# Revit family: Camera-Security-iPRO-2MP-Outdoor-PTZ-Network-Dome-AI-S65340-ZSeriesX
name_source: partatom
category: Security Devices
units: mm (PartAtom-declared; Revit-internal decimal feet)

## family parameters
Cut with Voids When Loaded = No
Host = Face
Maintain Annotation Orientation = No
OmniClass Number = 23.85.10.14.11
OmniClass Title = Cameras
Part Type = Normal
Room Calculation Point = No
Round Connector Dimension = Use Diameter
Shared = No

## types (3) — shared parameters
Alarm Input Or Output Specification = ALARM IN 1 (Alarm input 1/ Black & white input/ Auto time adjustment input) (x1) ALARM IN 2 (Alarm input 2/ ALARM OUT) (x1),  ARM IN 3 (Alarm input 3/ AUX OUT) (x1)
Audio In = Yes
Audio Out = Yes
Communication Ports = 10Base-T / 100Base-TX, RJ45 connector
Date Last Modified = 2022/08/05
Day Or Night = Yes
Diameter = 9.0157 "
Equipment Abbreviation = SC
Family Version = 1.0.0
Has POE = Yes
Height = 10.9449 "
IP Or Analog = IP
Indoor Or Outdoor = Outdoor
Manufacturer = i-PRO Co., Ltd.
Minimum Illumination = 0.015 lx
Model Disclaimer = Contact i-PRO for more information
Mounting Positions = Wall Mount
Operational Humidity = 10 to 100 % (no condensation)
Operational Temperature = -50 °C to +60 °C (-58 °F to +140 °F)
Pan Min = 0.00°
Product Documentation Link = https://bizpartner.panasonic.net
Product Material = Paint - i-Pro White
Product Page URL = https://i-pro.com
Provide Feedback = https://i-pro.com
Regulatory Compliance = UL (UL62368-1), c-UL (CSA C22.2 No.62368-1), CE, IEC62368-1, FCC (Part15 ClassA), ICES-003 Issue 7 ClassA, EN55032 ClassA, EN55035
Shock Resistance = IK10 (IEC 62262)
Storage Temperature = -50 °C to +60 °C (-58 °F to +140 °F)
Tilt Min = -15.00°
URL = https://i-pro.com
Vandal Resistant = Yes
Water and Dust Resistance = IP66, IP67, IEC60529 measuring standard compatible, Type 4X(UL50E), NEMA 4X compliant
Wide Dynamic Range = Yes
z Const Pan Handle Length = 27.5591 "
z Const Tilt Base Length = 14.1732 "
z Const Tilt Base2 Length = 19.685 "
z Const Tilt Handle Length = 14.1732 "
z Const Yaw Base Length = 9.8425 "
z Const Yaw Base2 Length = 500.00°
z Const Yaw Handle Length = 9.252 "
zero-valued in all types: Default Elevation

## per-type parameters (varying)
| type | Angle Of View | Description | HFOV Max 169 | HFOV Max 43 | HFOV Min 169 | HFOV Min 43 | Pan Max | Panning Range | Part Description | Tilt Max | Tilting Range | VFOV Max 169 | VFOV Max 43 | VFOV Min 169 | VFOV Min 43 | Weight | z Camera Type | z VV Viewpoint Depth Max | z VV Viewpoint Depth Min |
| WV-S65340-Z2N | 77 | Security Camera, 2MP ,21x,  Outdoor PTZ Network Camera with AI, WV-S65340-Z2N | 77.00° | 58.00° | 3.70° | 2.80° | 350.00° | 0 to +350 | Security Camera, 2MP ,21x,  Outdoor PTZ Network Camera with AI, WV-S65340-Z2N | 90.00° | -15 to +90 | 44.00° | 44.00° | 2.20° | 2.20° | 9.26 lb | 653402 | 1.6866 " | 1.6866 " |
| WV-S65340-Z4N | 65 | Security Camera, 2MP 40x Outdoor PTZ Network Camera  with AI, WV-S65340-Z4N | 65.00° | 51.00° | 2.10° | 1.60° | 360.00° | 360 | Security Camera, 2MP 40x Outdoor PTZ Network Camera  with AI, WV-S65340-Z4N | 195.00° | -15 to +195 | 39.00° | 39.00° | 1.20° | 1.20° | 9.48 lb | 653404 | 2.1076 " | 2.1076 " |
| WV-S65340-Z4K | 65 | Security Camera, Heavy-Duty Salt Damage-Resistant coating, 2MP 40x Outdoor PTZ Network with AI, WV-S65340-Z4K | 65.00° | 51.00° | 2.10° | 1.60° | 360.00° | 360 | Security Camera, Heavy-Duty Salt Damage-Resistant coating, 2MP 40x Outdoor PTZ Network with AI, WV-S65340-Z4K | 195.00° | -15 to +195 | 39.00° | 39.00° | 1.20° | 1.20° | 9.48 lb | 653404 | 2.1076 " | 2.1076 " |

note: column(s) folded — value = type name in every type: Model, Part Number

## geometry (parser evidence)
native form markers: Sweep x9
no freeform markers — native parametric forms only
